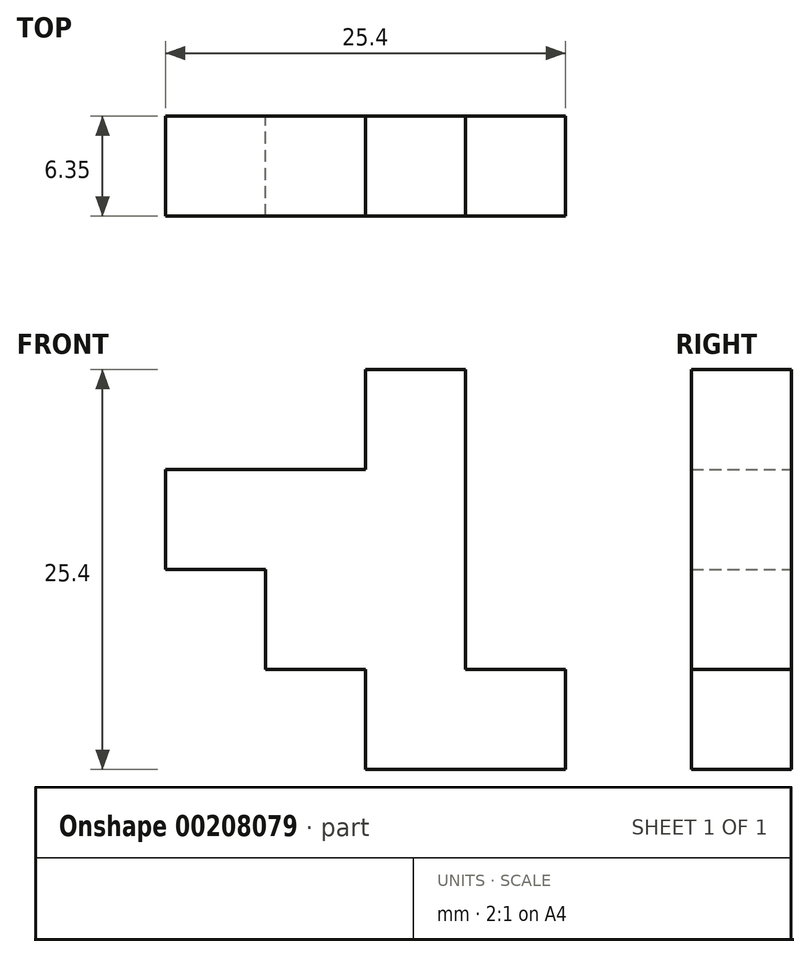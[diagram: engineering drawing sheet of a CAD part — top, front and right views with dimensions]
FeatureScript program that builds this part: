
annotation { "Feature Type Name" : "Feature", "Feature Type Description" : "" }
export const myFeature = defineFeature(function(context is Context, id is Id, definition is map)
    precondition{}
    {
        {
            var Q0;
            Q0=qCreatedBy(makeId("Front.planeOp"),FACE);
            var sketch = newSketch(context, id + "F0", { "sketchPlane" : qUnion([Q0])});
            skLineSegment(sketch, "E0.bottom", {"start": v(22.63, -12.09) * mm, "end": v(28.98, -12.09) * mm});
            skLineSegment(sketch, "E0.top", {"start": v(22.63, -37.49) * mm, "end": v(35.33, -37.49) * mm});
            skLineSegment(sketch, "E0.left", {"start": v(9.93, -18.44) * mm, "end": v(9.93, -24.79) * mm});
            skLineSegment(sketch, "E0.right", {"start": v(35.33, -31.14) * mm, "end": v(35.33, -37.49) * mm});
            skLineSegment(sketch, "E1", {"start": v(28.98, -12.09) * mm, "end": v(28.98, -31.14) * mm});
            skLineSegment(sketch, "E2", {"start": v(28.98, -31.14) * mm, "end": v(35.33, -31.14) * mm});
            skPoint(sketch, "E3.orphan", {"position": v(35.33, -12.09) * mm});
            skPoint(sketch, "E4.orphan", {"position": v(28.98, -37.49) * mm});
            skLineSegment(sketch, "E5", {"start": v(9.93, -18.44) * mm, "end": v(22.63, -18.44) * mm});
            skLineSegment(sketch, "E6", {"start": v(22.63, -18.44) * mm, "end": v(22.63, -12.09) * mm});
            skLineSegment(sketch, "E7", {"start": v(22.63, -31.14) * mm, "end": v(16.28, -31.14) * mm});
            skLineSegment(sketch, "E8", {"start": v(16.28, -24.79) * mm, "end": v(16.28, -31.14) * mm});
            skLineSegment(sketch, "E9", {"start": v(16.28, -24.79) * mm, "end": v(9.93, -24.79) * mm});
            skPoint(sketch, "E10.orphan", {"position": v(4.48, -24.79) * mm});
            skLineSegment(sketch, "E11", {"start": v(22.63, -37.49) * mm, "end": v(22.63, -31.14) * mm});
            skPoint(sketch, "E12.orphan", {"position": v(22.63, -39.28) * mm});
            skPoint(sketch, "E13.orphan", {"position": v(9.93, -37.49) * mm});
            skPoint(sketch, "E14.orphan", {"position": v(9.93, -31.14) * mm});
            skPoint(sketch, "E15.orphan", {"position": v(16.28, -18.44) * mm});
            skPoint(sketch, "E16.orphan", {"position": v(9.93, -12.09) * mm});
            skSolve(sketch);
        }
        {
            var Q0;
            Q0=makeQuery(id+"F0.imprint","IMPRINT",FACE,{"disambiguationData":[TD([[makeQuery(id+"F0.imprint","IMPRINT",EDGE,{"derivedFrom":sQuery(id+"F0.wireOp",EDGE,"E0.bottom")}),-1.0]])]});
            extrude(context, id + "F1", {"entities" : qUnion([Q0]), "depth" : 6.35 * mm});
        }
        {
            var Q0;
            Q0=makeQuery(id+"F0.imprint","IMPRINT",FACE,{"disambiguationData":[TD([[makeQuery(id+"F0.imprint","IMPRINT",EDGE,{"derivedFrom":sQuery(id+"F0.wireOp",EDGE,"E0.bottom")}),-1.0]])]});
            extrude(context, id + "F2", {"entities" : qUnion([Q0]), "depth" : 6.35 * mm});
        }
    });
